# Revit family: Haworth_JiveTable_RacetrackBases
name_source: partatom
category: Furniture Systems
revit_build: Autodesk Revit 2018 (Build: 20170223_1515(x64)
units: mm (PartAtom-declared; Revit-internal decimal feet)

## family parameters
Always vertical = Yes
Cut with Voids When Loaded = No
OmniClass Number = 23.40.70.14.64.21
OmniClass Title = Systems Furniture
Part Type = Normal
Room Calculation Point = No
Round Connector Dimension = Use Diameter
Shared = No
Work Plane-Based = No

## types (44) — shared parameters
4 Column = No
Assembly Code = E2020200
Manufacturer = Haworth, Inc.
Max. Depth = 54"
Max. Height = 42"
Max. Width = 180"
Min. Depth = 30"
Min. Height = 16"
Min. Width = 48"
Model = Haworth Jive
Revision Number = 0
Size = Verify Final Dim. w/ Haworth
Standard Depths = 30, 36, 42, 48, 54in.
Standard Heights = 16, 20, 29, 36, 42 in.
Standard Widths = 48, 60, 72, 84, 96, 108, 120, 144, 180 in.
Table Thickness = 1 3/16"
URL = https://www.haworth.com
URL - Product = http://www.haworth.com
Warranty = http://www.haworth.com
X Base = No

## per-type parameters (varying)
- 30d 48w 16h - Bridge Base - With Glides: 2 Column=Yes; 3 Column=No; 4 6 8 Column=No; 6 Column=No; 8 Column=No; Actual Depth=30"; Actual Height=16"; Actual Table Depth=48"; Actual Table Width=57"; Actual Width=48"; Bridge Distance=16 61/256"; Casters=No; Center Leg Location=0"; Columns=Yes; Custom Size=No; Depth=30"; Description=Haworth Jive Table Racetrack Bases - 30d 48w 16h - Bridge Base - With Glides; Glides=Yes; Height=16"; Leg Height=14 13/16"; Middle Columns=No; Support Depth 6 8 Column=4 29/32"; Support Distance=18 61/256"; Support Distance 6 8 Column=1 29/32"; Table Radius=15"; Width=48"; X Base 2 3 Column=Yes
- 30d 60w 16h - Bridge Base - With Glides: 2 Column=Yes; 3 Column=No; 4 6 8 Column=No; 6 Column=No; 8 Column=No; Actual Depth=30"; Actual Height=16"; Actual Table Depth=48"; Actual Table Width=60"; Actual Width=60"; Bridge Distance=26 5/256"; Casters=No; Center Leg Location=0"; Columns=Yes; Custom Size=No; Depth=30"; Description=Haworth Jive Table Racetrack Bases - 30d 60w 16h - Bridge Base - With Glides; Glides=Yes; Height=16"; Leg Height=14 13/16"; Middle Columns=No; Support Depth 6 8 Column=4 29/32"; Support Distance=28 5/256"; Support Distance 6 8 Column=4 29/32"; Table Radius=15"; Width=60"; X Base 2 3 Column=Yes
- 30d 72w 16h - Bridge Base - With Glides: 2 Column=Yes; 3 Column=No; 4 6 8 Column=No; 6 Column=No; 8 Column=No; Actual Depth=30"; Actual Height=16"; Actual Table Depth=48"; Actual Table Width=72"; Actual Width=72"; Bridge Distance=31 5/8"; Casters=No; Center Leg Location=0"; Columns=Yes; Custom Size=No; Depth=30"; Description=Haworth Jive Table Racetrack Bases - 30d 72w 16h - Bridge Base - With Glides; Glides=Yes; Height=16"; Leg Height=14 13/16"; Middle Columns=No; Support Depth 6 8 Column=4 29/32"; Support Distance=33 5/8"; Support Distance 6 8 Column=16 29/32"; Table Radius=15"; Width=72"; X Base 2 3 Column=Yes
- 36d 60w 16h - Bridge Base - With Glides: 2 Column=Yes; 3 Column=No; 4 6 8 Column=No; 6 Column=No; 8 Column=No; Actual Depth=36"; Actual Height=16"; Actual Table Depth=48"; Actual Table Width=60"; Actual Width=60"; Bridge Distance=26 5/256"; Casters=No; Center Leg Location=0"; Columns=Yes; Custom Size=No; Depth=36"; Description=Haworth Jive Table Racetrack Bases - 36d 60w 16h - Bridge Base - With Glides; Glides=Yes; Height=16"; Leg Height=14 13/16"; Middle Columns=No; Support Depth 6 8 Column=4 29/32"; Support Distance=28 5/256"; Support Distance 6 8 Column=4 29/32"; Table Radius=18"; Width=60"; X Base 2 3 Column=Yes
- 36d 72w 16h - Bridge Base - With Glides: 2 Column=Yes; 3 Column=No; 4 6 8 Column=No; 6 Column=No; 8 Column=No; Actual Depth=36"; Actual Height=16"; Actual Table Depth=48"; Actual Table Width=72"; Actual Width=72"; Bridge Distance=31 5/8"; Casters=No; Center Leg Location=0"; Columns=Yes; Custom Size=No; Depth=36"; Description=Haworth Jive Table Racetrack Bases - 36d 72w 16h - Bridge Base - With Glides; Glides=Yes; Height=16"; Leg Height=14 13/16"; Middle Columns=No; Support Depth 6 8 Column=4 29/32"; Support Distance=33 5/8"; Support Distance 6 8 Column=16 29/32"; Table Radius=18"; Width=72"; X Base 2 3 Column=Yes
- 30d 48w 20h - Bridge Base - With Glides: 2 Column=Yes; 3 Column=No; 4 6 8 Column=No; 6 Column=No; 8 Column=No; Actual Depth=30"; Actual Height=20"; Actual Table Depth=48"; Actual Table Width=57"; Actual Width=48"; Bridge Distance=16 61/256"; Casters=No; Center Leg Location=0"; Columns=Yes; Custom Size=No; Depth=30"; Description=Haworth Jive Table Racetrack Bases - 30d 48w 20h - Bridge Base - With Glides; Glides=Yes; Height=20"; Leg Height=18 13/16"; Middle Columns=No; Support Depth 6 8 Column=4 29/32"; Support Distance=18 61/256"; Support Distance 6 8 Column=1 29/32"; Table Radius=15"; Width=48"; X Base 2 3 Column=Yes
- 30d 60w 20h - Bridge Base - With Glides: 2 Column=Yes; 3 Column=No; 4 6 8 Column=No; 6 Column=No; 8 Column=No; Actual Depth=30"; Actual Height=20"; Actual Table Depth=48"; Actual Table Width=60"; Actual Width=60"; Bridge Distance=26 5/256"; Casters=No; Center Leg Location=0"; Columns=Yes; Custom Size=No; Depth=30"; Description=Haworth Jive Table Racetrack Bases - 30d 60w 20h - Bridge Base - With Glides; Glides=Yes; Height=20"; Leg Height=18 13/16"; Middle Columns=No; Support Depth 6 8 Column=4 29/32"; Support Distance=28 5/256"; Support Distance 6 8 Column=4 29/32"; Table Radius=15"; Width=60"; X Base 2 3 Column=Yes
- 30d 72w 20h - Bridge Base - With Glides: 2 Column=Yes; 3 Column=No; 4 6 8 Column=No; 6 Column=No; 8 Column=No; Actual Depth=30"; Actual Height=20"; Actual Table Depth=48"; Actual Table Width=72"; Actual Width=72"; Bridge Distance=31 5/8"; Casters=No; Center Leg Location=0"; Columns=Yes; Custom Size=No; Depth=30"; Description=Haworth Jive Table Racetrack Bases - 30d 72w 20h - Bridge Base - With Glides; Glides=Yes; Height=20"; Leg Height=18 13/16"; Middle Columns=No; Support Depth 6 8 Column=4 29/32"; Support Distance=33 5/8"; Support Distance 6 8 Column=16 29/32"; Table Radius=15"; Width=72"; X Base 2 3 Column=Yes
- 36d 60w 20h - Bridge Base - With Glides: 2 Column=Yes; 3 Column=No; 4 6 8 Column=No; 6 Column=No; 8 Column=No; Actual Depth=36"; Actual Height=20"; Actual Table Depth=48"; Actual Table Width=60"; Actual Width=60"; Bridge Distance=26 5/256"; Casters=No; Center Leg Location=0"; Columns=Yes; Custom Size=No; Depth=36"; Description=Haworth Jive Table Racetrack Bases - 36d 60w 20h - Bridge Base - With Glides; Glides=Yes; Height=20"; Leg Height=18 13/16"; Middle Columns=No; Support Depth 6 8 Column=4 29/32"; Support Distance=28 5/256"; Support Distance 6 8 Column=4 29/32"; Table Radius=18"; Width=60"; X Base 2 3 Column=Yes
- 36d 72w 20h - Bridge Base - With Glides: 2 Column=Yes; 3 Column=No; 4 6 8 Column=No; 6 Column=No; 8 Column=No; Actual Depth=36"; Actual Height=20"; Actual Table Depth=48"; Actual Table Width=72"; Actual Width=72"; Bridge Distance=31 5/8"; Casters=No; Center Leg Location=0"; Columns=Yes; Custom Size=No; Depth=36"; Description=Haworth Jive Table Racetrack Bases - 36d 72w 20h - Bridge Base - With Glides; Glides=Yes; Height=20"; Leg Height=18 13/16"; Middle Columns=No; Support Depth 6 8 Column=4 29/32"; Support Distance=33 5/8"; Support Distance 6 8 Column=16 29/32"; Table Radius=18"; Width=72"; X Base 2 3 Column=Yes
- 30d 48w 29h - Bridge Base - With Casters: 2 Column=Yes; 3 Column=No; 4 6 8 Column=No; 6 Column=No; 8 Column=No; Actual Depth=30"; Actual Height=29"; Actual Table Depth=48"; Actual Table Width=57"; Actual Width=48"; Bridge Distance=16 61/256"; Casters=Yes; Center Leg Location=0"; Columns=Yes; Custom Size=No; Depth=30"; Description=Haworth Jive Table Racetrack Bases - 30d 48w 29h - Bridge Base - With Casters; Glides=No; Height=29"; Leg Height=27 13/16"; Middle Columns=No; Support Depth 6 8 Column=4 29/32"; Support Distance=18 61/256"; Support Distance 6 8 Column=1 29/32"; Table Radius=15"; Width=48"; X Base 2 3 Column=Yes
- 30d 60w 29h - Bridge Base - With Casters: 2 Column=Yes; 3 Column=No; 4 6 8 Column=No; 6 Column=No; 8 Column=No; Actual Depth=30"; Actual Height=29"; Actual Table Depth=48"; Actual Table Width=60"; Actual Width=60"; Bridge Distance=26 5/256"; Casters=Yes; Center Leg Location=0"; Columns=Yes; Custom Size=No; Depth=30"; Description=Haworth Jive Table Racetrack Bases - 30d 60w 29h - Bridge Base - With Casters; Glides=No; Height=29"; Leg Height=27 13/16"; Middle Columns=No; Support Depth 6 8 Column=4 29/32"; Support Distance=28 5/256"; Support Distance 6 8 Column=4 29/32"; Table Radius=15"; Width=60"; X Base 2 3 Column=Yes
- 30d 72w 29h - Bridge Base - With Casters: 2 Column=Yes; 3 Column=No; 4 6 8 Column=No; 6 Column=No; 8 Column=No; Actual Depth=30"; Actual Height=29"; Actual Table Depth=48"; Actual Table Width=72"; Actual Width=72"; Bridge Distance=31 5/8"; Casters=Yes; Center Leg Location=0"; Columns=Yes; Custom Size=No; Depth=30"; Description=Haworth Jive Table Racetrack Bases - 30d 72w 29h - Bridge Base - With Casters; Glides=No; Height=29"; Leg Height=27 13/16"; Middle Columns=No; Support Depth 6 8 Column=4 29/32"; Support Distance=33 5/8"; Support Distance 6 8 Column=16 29/32"; Table Radius=15"; Width=72"; X Base 2 3 Column=Yes
- 36d 60w 29h - Bridge Base - With Casters: 2 Column=Yes; 3 Column=No; 4 6 8 Column=No; 6 Column=No; 8 Column=No; Actual Depth=36"; Actual Height=29"; Actual Table Depth=48"; Actual Table Width=60"; Actual Width=60"; Bridge Distance=26 5/256"; Casters=Yes; Center Leg Location=0"; Columns=Yes; Custom Size=No; Depth=36"; Description=Haworth Jive Table Racetrack Bases - 36d 60w 29h - Bridge Base - With Casters; Glides=No; Height=29"; Leg Height=27 13/16"; Middle Columns=No; Support Depth 6 8 Column=4 29/32"; Support Distance=28 5/256"; Support Distance 6 8 Column=4 29/32"; Table Radius=18"; Width=60"; X Base 2 3 Column=Yes
- 36d 72w 29h - Bridge Base - With Casters: 2 Column=Yes; 3 Column=No; 4 6 8 Column=No; 6 Column=No; 8 Column=No; Actual Depth=36"; Actual Height=29"; Actual Table Depth=48"; Actual Table Width=72"; Actual Width=72"; Bridge Distance=31 5/8"; Casters=Yes; Center Leg Location=0"; Columns=Yes; Custom Size=No; Depth=36"; Description=Haworth Jive Table Racetrack Bases - 36d 72w 29h - Bridge Base - With Casters; Glides=No; Height=29"; Leg Height=27 13/16"; Middle Columns=No; Support Depth 6 8 Column=4 29/32"; Support Distance=33 5/8"; Support Distance 6 8 Column=16 29/32"; Table Radius=18"; Width=72"; X Base 2 3 Column=Yes
- 30d 48w 29h - Bridge Base - With Glides: 2 Column=Yes; 3 Column=No; 4 6 8 Column=No; 6 Column=No; 8 Column=No; Actual Depth=30"; Actual Height=29"; Actual Table Depth=48"; Actual Table Width=57"; Actual Width=48"; Bridge Distance=16 61/256"; Casters=No; Center Leg Location=0"; Columns=Yes; Custom Size=No; Depth=30"; Description=Haworth Jive Table Racetrack Bases - 30d 48w 29h - Bridge Base - With Glides; Glides=Yes; Height=29"; Leg Height=27 13/16"; Middle Columns=No; Support Depth 6 8 Column=4 29/32"; Support Distance=18 61/256"; Support Distance 6 8 Column=1 29/32"; Table Radius=15"; Width=48"; X Base 2 3 Column=Yes
- 30d 60w 29h - Bridge Base - With Glides: 2 Column=Yes; 3 Column=No; 4 6 8 Column=No; 6 Column=No; 8 Column=No; Actual Depth=30"; Actual Height=29"; Actual Table Depth=48"; Actual Table Width=60"; Actual Width=60"; Bridge Distance=26 5/256"; Casters=No; Center Leg Location=0"; Columns=Yes; Custom Size=No; Depth=30"; Description=Haworth Jive Table Racetrack Bases - 30d 60w 29h - Bridge Base - With Glides; Glides=Yes; Height=29"; Leg Height=27 13/16"; Middle Columns=No; Support Depth 6 8 Column=4 29/32"; Support Distance=28 5/256"; Support Distance 6 8 Column=4 29/32"; Table Radius=15"; Width=60"; X Base 2 3 Column=Yes
- 30d 72w 29h - Bridge Base - With Glides: 2 Column=Yes; 3 Column=No; 4 6 8 Column=No; 6 Column=No; 8 Column=No; Actual Depth=30"; Actual Height=29"; Actual Table Depth=48"; Actual Table Width=72"; Actual Width=72"; Bridge Distance=31 5/8"; Casters=No; Center Leg Location=0"; Columns=Yes; Custom Size=No; Depth=30"; Description=Haworth Jive Table Racetrack Bases - 30d 72w 29h - Bridge Base - With Glides; Glides=Yes; Height=29"; Leg Height=27 13/16"; Middle Columns=No; Support Depth 6 8 Column=4 29/32"; Support Distance=33 5/8"; Support Distance 6 8 Column=16 29/32"; Table Radius=15"; Width=72"; X Base 2 3 Column=Yes
- 36d 60w 29h - Bridge Base - With Glides: 2 Column=Yes; 3 Column=No; 4 6 8 Column=No; 6 Column=No; 8 Column=No; Actual Depth=36"; Actual Height=29"; Actual Table Depth=48"; Actual Table Width=60"; Actual Width=60"; Bridge Distance=26 5/256"; Casters=No; Center Leg Location=0"; Columns=Yes; Custom Size=No; Depth=36"; Description=Haworth Jive Table Racetrack Bases - 36d 60w 29h - Bridge Base - With Glides; Glides=Yes; Height=29"; Leg Height=27 13/16"; Middle Columns=No; Support Depth 6 8 Column=4 29/32"; Support Distance=28 5/256"; Support Distance 6 8 Column=4 29/32"; Table Radius=18"; Width=60"; X Base 2 3 Column=Yes
- 36d 72w 29h - Bridge Base - With Glides: 2 Column=Yes; 3 Column=No; 4 6 8 Column=No; 6 Column=No; 8 Column=No; Actual Depth=36"; Actual Height=29"; Actual Table Depth=48"; Actual Table Width=72"; Actual Width=72"; Bridge Distance=31 5/8"; Casters=No; Center Leg Location=0"; Columns=Yes; Custom Size=No; Depth=36"; Description=Haworth Jive Table Racetrack Bases - 36d 72w 29h - Bridge Base - With Glides; Glides=Yes; Height=29"; Leg Height=27 13/16"; Middle Columns=No; Support Depth 6 8 Column=4 29/32"; Support Distance=33 5/8"; Support Distance 6 8 Column=16 29/32"; Table Radius=18"; Width=72"; X Base 2 3 Column=Yes
- 30d 48w 36h - Bridge Base - With Glides: 2 Column=Yes; 3 Column=No; 4 6 8 Column=No; 6 Column=No; 8 Column=No; Actual Depth=30"; Actual Height=36"; Actual Table Depth=48"; Actual Table Width=57"; Actual Width=48"; Bridge Distance=16 61/256"; Casters=No; Center Leg Location=0"; Columns=Yes; Custom Size=No; Depth=30"; Description=Haworth Jive Table Racetrack Bases - 30d 48w 36h - Bridge Base - With Glides; Glides=Yes; Height=36"; Leg Height=34 13/16"; Middle Columns=No; Support Depth 6 8 Column=4 29/32"; Support Distance=18 61/256"; Support Distance 6 8 Column=1 29/32"; Table Radius=15"; Width=48"; X Base 2 3 Column=Yes
- 30d 60w 36h - Bridge Base - With Glides: 2 Column=Yes; 3 Column=No; 4 6 8 Column=No; 6 Column=No; 8 Column=No; Actual Depth=30"; Actual Height=36"; Actual Table Depth=48"; Actual Table Width=60"; Actual Width=60"; Bridge Distance=26 5/256"; Casters=No; Center Leg Location=0"; Columns=Yes; Custom Size=No; Depth=30"; Description=Haworth Jive Table Racetrack Bases - 30d 60w 36h - Bridge Base - With Glides; Glides=Yes; Height=36"; Leg Height=34 13/16"; Middle Columns=No; Support Depth 6 8 Column=4 29/32"; Support Distance=28 5/256"; Support Distance 6 8 Column=4 29/32"; Table Radius=15"; Width=60"; X Base 2 3 Column=Yes
- 30d 72w 36h - Bridge Base - With Glides: 2 Column=Yes; 3 Column=No; 4 6 8 Column=No; 6 Column=No; 8 Column=No; Actual Depth=30"; Actual Height=36"; Actual Table Depth=48"; Actual Table Width=72"; Actual Width=72"; Bridge Distance=31 5/8"; Casters=No; Center Leg Location=0"; Columns=Yes; Custom Size=No; Depth=30"; Description=Haworth Jive Table Racetrack Bases - 30d 72w 36h - Bridge Base - With Glides; Glides=Yes; Height=36"; Leg Height=34 13/16"; Middle Columns=No; Support Depth 6 8 Column=4 29/32"; Support Distance=33 5/8"; Support Distance 6 8 Column=16 29/32"; Table Radius=15"; Width=72"; X Base 2 3 Column=Yes
- 36d 60w 36h - Bridge Base - With Glides: 2 Column=Yes; 3 Column=No; 4 6 8 Column=No; 6 Column=No; 8 Column=No; Actual Depth=36"; Actual Height=36"; Actual Table Depth=48"; Actual Table Width=60"; Actual Width=60"; Bridge Distance=26 5/256"; Casters=No; Center Leg Location=0"; Columns=Yes; Custom Size=No; Depth=36"; Description=Haworth Jive Table Racetrack Bases - 36d 60w 36h - Bridge Base - With Glides; Glides=Yes; Height=36"; Leg Height=34 13/16"; Middle Columns=No; Support Depth 6 8 Column=4 29/32"; Support Distance=28 5/256"; Support Distance 6 8 Column=4 29/32"; Table Radius=18"; Width=60"; X Base 2 3 Column=Yes
- 36d 72w 36h - Bridge Base - With Glides: 2 Column=Yes; 3 Column=No; 4 6 8 Column=No; 6 Column=No; 8 Column=No; Actual Depth=36"; Actual Height=36"; Actual Table Depth=48"; Actual Table Width=72"; Actual Width=72"; Bridge Distance=31 5/8"; Casters=No; Center Leg Location=0"; Columns=Yes; Custom Size=No; Depth=36"; Description=Haworth Jive Table Racetrack Bases - 36d 72w 36h - Bridge Base - With Glides; Glides=Yes; Height=36"; Leg Height=34 13/16"; Middle Columns=No; Support Depth 6 8 Column=4 29/32"; Support Distance=33 5/8"; Support Distance 6 8 Column=16 29/32"; Table Radius=18"; Width=72"; X Base 2 3 Column=Yes
- 30d 48w 42h - Bridge Base - With Casters: 2 Column=Yes; 3 Column=No; 4 6 8 Column=No; 6 Column=No; 8 Column=No; Actual Depth=30"; Actual Height=42"; Actual Table Depth=48"; Actual Table Width=57"; Actual Width=48"; Bridge Distance=16 61/256"; Casters=Yes; Center Leg Location=0"; Columns=Yes; Custom Size=No; Depth=30"; Description=Haworth Jive Table Racetrack Bases - 30d 48w 42h - Bridge Base - With Casters; Glides=No; Height=42"; Leg Height=40 13/16"; Middle Columns=No; Support Depth 6 8 Column=4 29/32"; Support Distance=18 61/256"; Support Distance 6 8 Column=1 29/32"; Table Radius=15"; Width=48"; X Base 2 3 Column=Yes
- 30d 60w 42h - Bridge Base - With Casters: 2 Column=Yes; 3 Column=No; 4 6 8 Column=No; 6 Column=No; 8 Column=No; Actual Depth=30"; Actual Height=42"; Actual Table Depth=48"; Actual Table Width=60"; Actual Width=60"; Bridge Distance=26 5/256"; Casters=Yes; Center Leg Location=0"; Columns=Yes; Custom Size=No; Depth=30"; Description=Haworth Jive Table Racetrack Bases - 30d 60w 42h - Bridge Base - With Casters; Glides=No; Height=42"; Leg Height=40 13/16"; Middle Columns=No; Support Depth 6 8 Column=4 29/32"; Support Distance=28 5/256"; Support Distance 6 8 Column=4 29/32"; Table Radius=15"; Width=60"; X Base 2 3 Column=Yes
- 30d 72w 42h - Bridge Base - With Casters: 2 Column=Yes; 3 Column=No; 4 6 8 Column=No; 6 Column=No; 8 Column=No; Actual Depth=30"; Actual Height=42"; Actual Table Depth=48"; Actual Table Width=72"; Actual Width=72"; Bridge Distance=31 5/8"; Casters=Yes; Center Leg Location=0"; Columns=Yes; Custom Size=No; Depth=30"; Description=Haworth Jive Table Racetrack Bases - 30d 72w 42h - Bridge Base - With Casters; Glides=No; Height=42"; Leg Height=40 13/16"; Middle Columns=No; Support Depth 6 8 Column=4 29/32"; Support Distance=33 5/8"; Support Distance 6 8 Column=16 29/32"; Table Radius=15"; Width=72"; X Base 2 3 Column=Yes
- 36d 60w 42h - Bridge Base - With Casters: 2 Column=Yes; 3 Column=No; 4 6 8 Column=No; 6 Column=No; 8 Column=No; Actual Depth=36"; Actual Height=42"; Actual Table Depth=48"; Actual Table Width=60"; Actual Width=60"; Bridge Distance=26 5/256"; Casters=Yes; Center Leg Location=0"; Columns=Yes; Custom Size=No; Depth=36"; Description=Haworth Jive Table Racetrack Bases - 36d 60w 42h - Bridge Base - With Casters; Glides=No; Height=42"; Leg Height=40 13/16"; Middle Columns=No; Support Depth 6 8 Column=4 29/32"; Support Distance=28 5/256"; Support Distance 6 8 Column=4 29/32"; Table Radius=18"; Width=60"; X Base 2 3 Column=Yes
- 36d 72w 42h - Bridge Base - With Casters: 2 Column=Yes; 3 Column=No; 4 6 8 Column=No; 6 Column=No; 8 Column=No; Actual Depth=36"; Actual Height=42"; Actual Table Depth=48"; Actual Table Width=72"; Actual Width=72"; Bridge Distance=31 5/8"; Casters=Yes; Center Leg Location=0"; Columns=Yes; Custom Size=No; Depth=36"; Description=Haworth Jive Table Racetrack Bases - 36d 72w 42h - Bridge Base - With Casters; Glides=No; Height=42"; Leg Height=40 13/16"; Middle Columns=No; Support Depth 6 8 Column=4 29/32"; Support Distance=33 5/8"; Support Distance 6 8 Column=16 29/32"; Table Radius=18"; Width=72"; X Base 2 3 Column=Yes
- 30d 48w 42h - Bridge Base - With Glides: 2 Column=Yes; 3 Column=No; 4 6 8 Column=No; 6 Column=No; 8 Column=No; Actual Depth=30"; Actual Height=42"; Actual Table Depth=48"; Actual Table Width=57"; Actual Width=48"; Bridge Distance=16 61/256"; Casters=No; Center Leg Location=0"; Columns=Yes; Custom Size=No; Depth=30"; Description=Haworth Jive Table Racetrack Bases - 30d 48w 42h - Bridge Base - With Glides; Glides=Yes; Height=42"; Leg Height=40 13/16"; Middle Columns=No; Support Depth 6 8 Column=4 29/32"; Support Distance=18 61/256"; Support Distance 6 8 Column=1 29/32"; Table Radius=15"; Width=48"; X Base 2 3 Column=Yes
- 30d 60w 42h - Bridge Base - With Glides: 2 Column=Yes; 3 Column=No; 4 6 8 Column=No; 6 Column=No; 8 Column=No; Actual Depth=30"; Actual Height=42"; Actual Table Depth=48"; Actual Table Width=60"; Actual Width=60"; Bridge Distance=26 5/256"; Casters=No; Center Leg Location=0"; Columns=Yes; Custom Size=No; Depth=30"; Description=Haworth Jive Table Racetrack Bases - 30d 60w 42h - Bridge Base - With Glides; Glides=Yes; Height=42"; Leg Height=40 13/16"; Middle Columns=No; Support Depth 6 8 Column=4 29/32"; Support Distance=28 5/256"; Support Distance 6 8 Column=4 29/32"; Table Radius=15"; Width=60"; X Base 2 3 Column=Yes
- 30d 72w 42h - Bridge Base - With Glides: 2 Column=Yes; 3 Column=No; 4 6 8 Column=No; 6 Column=No; 8 Column=No; Actual Depth=30"; Actual Height=42"; Actual Table Depth=48"; Actual Table Width=72"; Actual Width=72"; Bridge Distance=31 5/8"; Casters=No; Center Leg Location=0"; Columns=Yes; Custom Size=No; Depth=30"; Description=Haworth Jive Table Racetrack Bases - 30d 72w 42h - Bridge Base - With Glides; Glides=Yes; Height=42"; Leg Height=40 13/16"; Middle Columns=No; Support Depth 6 8 Column=4 29/32"; Support Distance=33 5/8"; Support Distance 6 8 Column=16 29/32"; Table Radius=15"; Width=72"; X Base 2 3 Column=Yes
- 36d 60w 42h - Bridge Base - With Glides: 2 Column=Yes; 3 Column=No; 4 6 8 Column=No; 6 Column=No; 8 Column=No; Actual Depth=36"; Actual Height=42"; Actual Table Depth=48"; Actual Table Width=60"; Actual Width=60"; Bridge Distance=26 5/256"; Casters=No; Center Leg Location=0"; Columns=Yes; Custom Size=No; Depth=36"; Description=Haworth Jive Table Racetrack Bases - 36d 60w 42h - Bridge Base - With Glides; Glides=Yes; Height=42"; Leg Height=40 13/16"; Middle Columns=No; Support Depth 6 8 Column=4 29/32"; Support Distance=28 5/256"; Support Distance 6 8 Column=4 29/32"; Table Radius=18"; Width=60"; X Base 2 3 Column=Yes
- 36d 72w 42h - Bridge Base - With Glides: 2 Column=Yes; 3 Column=No; 4 6 8 Column=No; 6 Column=No; 8 Column=No; Actual Depth=36"; Actual Height=42"; Actual Table Depth=48"; Actual Table Width=72"; Actual Width=72"; Bridge Distance=31 5/8"; Casters=No; Center Leg Location=0"; Columns=Yes; Custom Size=No; Depth=36"; Description=Haworth Jive Table Racetrack Bases - 36d 72w 42h - Bridge Base - With Glides; Glides=Yes; Height=42"; Leg Height=40 13/16"; Middle Columns=No; Support Depth 6 8 Column=4 29/32"; Support Distance=33 5/8"; Support Distance 6 8 Column=16 29/32"; Table Radius=18"; Width=72"; X Base 2 3 Column=Yes
- 42d 84w 29h - Bridge Base - With Glides: 2 Column=No; 3 Column=No; 4 6 8 Column=Yes; 6 Column=No; 8 Column=No; Actual Depth=42"; Actual Height=29"; Actual Table Depth=48"; Actual Table Width=84"; Actual Width=84"; Bridge Distance=37 29/128"; Casters=No; Center Leg Location=0"; Columns=No; Custom Size=Yes; Depth=42"; Description=Haworth Jive Table Racetrack Bases - 42d 84w 29h - Bridge Base - With Glides; Glides=Yes; Height=29"; Leg Height=27 13/16"; Middle Columns=No; Support Depth 6 8 Column=4 29/32"; Support Distance=39 29/128"; Support Distance 6 8 Column=28 29/32"; Table Radius=21"; Width=84"; X Base 2 3 Column=No
- 42d 96w 29h - Bridge Base - With Glides: 2 Column=No; 3 Column=No; 4 6 8 Column=Yes; 6 Column=No; 8 Column=No; Actual Depth=42"; Actual Height=29"; Actual Table Depth=48"; Actual Table Width=96"; Actual Width=96"; Bridge Distance=42 213/256"; Casters=No; Center Leg Location=0"; Columns=No; Custom Size=Yes; Depth=42"; Description=Haworth Jive Table Racetrack Bases - 42d 96w 29h - Bridge Base - With Glides; Glides=Yes; Height=29"; Leg Height=27 13/16"; Middle Columns=No; Support Depth 6 8 Column=4 29/32"; Support Distance=44 213/256"; Support Distance 6 8 Column=40 29/32"; Table Radius=21"; Width=96"; X Base 2 3 Column=No
- 48d 108w 29h - Bridge Base - With Glides: 2 Column=No; 3 Column=Yes; 4 6 8 Column=No; 6 Column=No; 8 Column=No; Actual Depth=48"; Actual Height=29"; Actual Table Depth=48"; Actual Table Width=108"; Actual Width=108"; Bridge Distance=48 7/16"; Casters=No; Center Leg Location=0"; Columns=Yes; Custom Size=No; Depth=48"; Description=Haworth Jive Table Racetrack Bases - 48d 108w 29h - Bridge Base - With Glides; Glides=Yes; Height=29"; Leg Height=27 13/16"; Middle Columns=No; Support Depth 6 8 Column=4 29/32"; Support Distance=50 7/16"; Support Distance 6 8 Column=52 29/32"; Table Radius=24"; Width=108"; X Base 2 3 Column=Yes
- 48d 120w 29h - Bridge Base - With Glides: 2 Column=No; 3 Column=Yes; 4 6 8 Column=No; 6 Column=No; 8 Column=No; Actual Depth=48"; Actual Height=29"; Actual Table Depth=48"; Actual Table Width=120"; Actual Width=120"; Bridge Distance=54 5/128"; Casters=No; Center Leg Location=0"; Columns=Yes; Custom Size=No; Depth=48"; Description=Haworth Jive Table Racetrack Bases - 48d 120w 29h - Bridge Base - With Glides; Glides=Yes; Height=29"; Leg Height=27 13/16"; Middle Columns=No; Support Depth 6 8 Column=4 29/32"; Support Distance=56 5/128"; Support Distance 6 8 Column=64 29/32"; Table Radius=24"; Width=120"; X Base 2 3 Column=Yes
- 54d 96w 29h - Bridge Base - With Glides: 2 Column=No; 3 Column=No; 4 6 8 Column=Yes; 6 Column=No; 8 Column=No; Actual Depth=54"; Actual Height=29"; Actual Table Depth=54"; Actual Table Width=96"; Actual Width=96"; Bridge Distance=42 213/256"; Casters=No; Center Leg Location=0"; Columns=No; Custom Size=Yes; Depth=54"; Description=Haworth Jive Table Racetrack Bases - 54d 96w 29h - Bridge Base - With Glides; Glides=Yes; Height=29"; Leg Height=27 13/16"; Middle Columns=No; Support Depth 6 8 Column=10 29/32"; Support Distance=44 213/256"; Support Distance 6 8 Column=40 29/32"; Table Radius=27"; Width=96"; X Base 2 3 Column=No
- 54d 108w 29h - Bridge Base - With Glides: 2 Column=No; 3 Column=No; 4 6 8 Column=Yes; 6 Column=Yes; 8 Column=No; Actual Depth=54"; Actual Height=29"; Actual Table Depth=54"; Actual Table Width=108"; Actual Width=108"; Bridge Distance=48 7/16"; Casters=No; Center Leg Location=0"; Columns=No; Custom Size=No; Depth=54"; Description=Haworth Jive Table Racetrack Bases - 54d 108w 29h - Bridge Base - With Glides; Glides=Yes; Height=29"; Leg Height=27 13/16"; Middle Columns=Yes; Support Depth 6 8 Column=10 29/32"; Support Distance=50 7/16"; Support Distance 6 8 Column=52 29/32"; Table Radius=27"; Width=108"; X Base 2 3 Column=No
- 54d 120w 29h - Bridge Base - With Glides: 2 Column=No; 3 Column=No; 4 6 8 Column=Yes; 6 Column=Yes; 8 Column=No; Actual Depth=54"; Actual Height=29"; Actual Table Depth=54"; Actual Table Width=120"; Actual Width=120"; Bridge Distance=54 5/128"; Casters=No; Center Leg Location=0"; Columns=No; Custom Size=No; Depth=54"; Description=Haworth Jive Table Racetrack Bases - 54d 120w 29h - Bridge Base - With Glides; Glides=Yes; Height=29"; Leg Height=27 13/16"; Middle Columns=Yes; Support Depth 6 8 Column=10 29/32"; Support Distance=56 5/128"; Support Distance 6 8 Column=64 29/32"; Table Radius=27"; Width=120"; X Base 2 3 Column=No
- 54d 144w 29h - Bridge Base - With Glides: 2 Column=No; 3 Column=No; 4 6 8 Column=Yes; 6 Column=Yes; 8 Column=No; Actual Depth=54"; Actual Height=29"; Actual Table Depth=54"; Actual Table Width=144"; Actual Width=144"; Bridge Distance=65 63/256"; Casters=No; Center Leg Location=0"; Columns=No; Custom Size=No; Depth=54"; Description=Haworth Jive Table Racetrack Bases - 54d 144w 29h - Bridge Base - With Glides; Glides=Yes; Height=29"; Leg Height=27 13/16"; Middle Columns=Yes; Support Depth 6 8 Column=10 29/32"; Support Distance=67 63/256"; Support Distance 6 8 Column=88 29/32"; Table Radius=27"; Width=144"; X Base 2 3 Column=No
- 54d 180w 29h - Bridge Base - With Glides: 2 Column=No; 3 Column=No; 4 6 8 Column=Yes; 6 Column=No; 8 Column=Yes; Actual Depth=54"; Actual Height=29"; Actual Table Depth=54"; Actual Table Width=180"; Actual Width=180"; Bridge Distance=82 15/256"; Casters=No; Center Leg Location=21"; Columns=No; Custom Size=No; Depth=54"; Description=Haworth Jive Table Racetrack Bases - 54d 180w 29h - Bridge Base - With Glides; Glides=Yes; Height=29"; Leg Height=27 13/16"; Middle Columns=Yes; Support Depth 6 8 Column=10 29/32"; Support Distance=84 15/256"; Support Distance 6 8 Column=124 29/32"; Table Radius=27"; Width=180"; X Base 2 3 Column=No

## geometry (parser evidence)
native form markers: Sweep x33
no freeform markers — native parametric forms only
